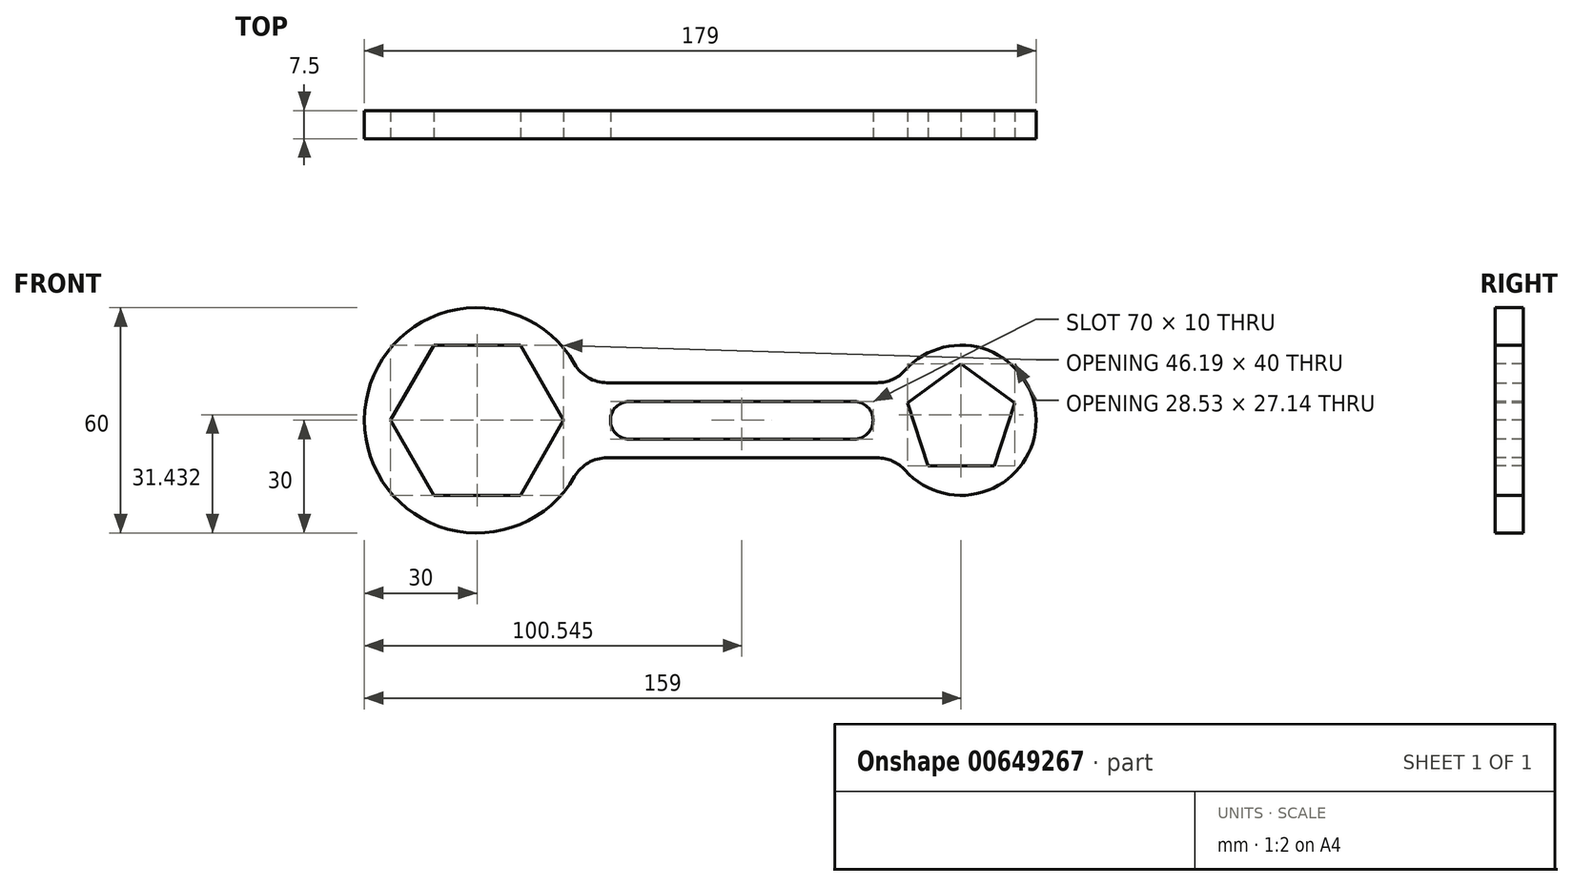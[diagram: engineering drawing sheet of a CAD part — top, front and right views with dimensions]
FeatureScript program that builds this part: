
annotation { "Feature Type Name" : "Feature", "Feature Type Description" : "" }
export const myFeature = defineFeature(function(context is Context, id is Id, definition is map)
    precondition{}
    {
        {
            var Q0;
            Q0=qCreatedBy(makeId("Front.planeOp"),FACE);
            var sketch = newSketch(context, id + "F0", { "sketchPlane" : qUnion([Q0])});
            skLineSegment(sketch, "E0.bottom", {"start": v(-64.5, 10) * mm, "end": v(64.5, 10) * mm});
            skLineSegment(sketch, "E0.top", {"start": v(-64.5, -10) * mm, "end": v(64.5, -10) * mm});
            skLineSegment(sketch, "E0.left", {"start": v(-64.5, 10) * mm, "end": v(-64.5, -10) * mm});
            skLineSegment(sketch, "E0.right", {"start": v(64.5, 10) * mm, "end": v(64.5, -10) * mm});
            skPoint(sketch, "E0.middle", {"position": v(0, 0) * mm});
            skCircle(sketch, "E1", {"center": v(-64.5, 0) * mm, "radius": 30 * mm});
            skCircle(sketch, "E2", {"center": v(64.5, 0) * mm, "radius": 20 * mm});
            skSolve(sketch);
        }
        {
            var Q0;
            Q0 = qSketchRegion(id + "F0", true);
            extrude(context, id + "F1", {"entities" : qUnion([Q0]), "depth" : 7.5 * mm, "offsetDistance" : 25 * mm});
        }
        {
            var Q0;
            Q0=makeQuery(id+"F1.opExtrude","CAP_FACE",FACE,{"disambiguationData":[OSD([sQuery(id+"F0.wireOp",EDGE,"E0.bottom"),sQuery(id+"F0.wireOp",EDGE,"E0.top"),sQuery(id+"F0.wireOp",EDGE,"E1"),sQuery(id+"F0.wireOp",EDGE,"E2")])],"isStart":false});
            var sketch = newSketch(context, id + "F2", { "sketchPlane" : qUnion([Q0])});
            skPoint(sketch, "E3", {"position": v(-64.5, 0) * mm});
            skCircle(sketch, "E4.cCircle", {"center": v(-64.5, 0) * mm, "radius": 20 * mm, "construction": true});
            skLineSegment(sketch, "E4.0", {"start": v(-76.05, 20) * mm, "end": v(-52.95, 20) * mm});
            skLineSegment(sketch, "E4.1", {"start": v(-52.95, 20) * mm, "end": v(-41.4, 0) * mm});
            skLineSegment(sketch, "E4.2", {"start": v(-41.4, 0) * mm, "end": v(-52.95, -20) * mm});
            skLineSegment(sketch, "E4.3", {"start": v(-52.95, -20) * mm, "end": v(-76.05, -20) * mm});
            skLineSegment(sketch, "E4.4", {"start": v(-76.05, -20) * mm, "end": v(-87.6, 0) * mm});
            skLineSegment(sketch, "E4.5", {"start": v(-87.6, 0) * mm, "end": v(-76.05, 20) * mm});
            skPoint(sketch, "E4.0.midPoint", {"position": v(-64.5, 20) * mm});
            skSolve(sketch);
        }
        {
            var Q0;
            Q0 = qSketchRegion(id + "F2", true);
            extrude(context, id + "F3", {"entities" : qUnion([Q0]), "operationType" : NewBodyOperationType.REMOVE, "oppositeDirection" : true, "depth" : 25 * mm, "offsetDistance" : 25 * mm});
        }
        {
            var Q0;
            Q0=makeQuery(id+"F1.opExtrude","CAP_FACE",FACE,{"disambiguationData":[OSD([sQuery(id+"F0.wireOp",EDGE,"E0.bottom"),sQuery(id+"F0.wireOp",EDGE,"E0.top"),sQuery(id+"F0.wireOp",EDGE,"E1"),sQuery(id+"F0.wireOp",EDGE,"E2")])],"isStart":false});
            var sketch = newSketch(context, id + "F4", { "sketchPlane" : qUnion([Q0])});
            skPoint(sketch, "E5", {"position": v(64.5, 0) * mm});
            skCircle(sketch, "E6.cCircle", {"center": v(64.5, 0) * mm, "radius": 12.14 * mm, "construction": true});
            skLineSegment(sketch, "E6.0", {"start": v(78.77, 4.64) * mm, "end": v(73.32, -12.14) * mm});
            skLineSegment(sketch, "E6.1", {"start": v(73.32, -12.14) * mm, "end": v(55.68, -12.14) * mm});
            skLineSegment(sketch, "E6.2", {"start": v(55.68, -12.14) * mm, "end": v(50.23, 4.64) * mm});
            skLineSegment(sketch, "E6.3", {"start": v(50.23, 4.64) * mm, "end": v(64.5, 15) * mm});
            skLineSegment(sketch, "E6.4", {"start": v(64.5, 15) * mm, "end": v(78.77, 4.64) * mm});
            skPoint(sketch, "E6.0.midPoint", {"position": v(76.04, -3.75) * mm});
            skSolve(sketch);
        }
        {
            var Q0;
            Q0 = qSketchRegion(id + "F4", true);
            extrude(context, id + "F5", {"entities" : qUnion([Q0]), "operationType" : NewBodyOperationType.REMOVE, "oppositeDirection" : true, "depth" : 25 * mm, "offsetDistance" : 25 * mm});
        }
        {
            var Q0;
            Q0=makeQuery(id+"F1.opExtrude","CAP_FACE",FACE,{"disambiguationData":[OSD([sQuery(id+"F0.wireOp",EDGE,"E0.bottom"),sQuery(id+"F0.wireOp",EDGE,"E0.top"),sQuery(id+"F0.wireOp",EDGE,"E1"),sQuery(id+"F0.wireOp",EDGE,"E2")])],"isStart":false});
            var sketch = newSketch(context, id + "F6", { "sketchPlane" : qUnion([Q0])});
            skLineSegment(sketch, "E7.bottom", {"start": v(-23.95, -5) * mm, "end": v(36.05, -5) * mm});
            skLineSegment(sketch, "E7.top", {"start": v(-23.95, 5) * mm, "end": v(36.05, 5) * mm});
            skLineSegment(sketch, "E7.left", {"start": v(-23.95, -5) * mm, "end": v(-23.95, 5) * mm});
            skLineSegment(sketch, "E7.right", {"start": v(36.05, -5) * mm, "end": v(36.05, 5) * mm});
            skPoint(sketch, "E7.middle", {"position": v(6.05, 0) * mm});
            skArc(sketch, "E8", {"start": v(36.05, -5) * mm, "mid": v(41.05, 0) * mm, "end": v(36.05, 5) * mm});
            skArc(sketch, "E9", {"start": v(-23.95, 5) * mm, "mid": v(-28.95, 0) * mm, "end": v(-23.95, -5) * mm});
            skSolve(sketch);
        }
        {
            var Q0;
            Q0 = qSketchRegion(id + "F6", true);
            extrude(context, id + "F7", {"entities" : qUnion([Q0]), "operationType" : NewBodyOperationType.REMOVE, "oppositeDirection" : true, "depth" : 25 * mm, "offsetDistance" : 25 * mm});
        }
        {
            var Q0;
            Q0=makeQuery(id+"F1.opExtrude","SWEPT_EDGE",EDGE,{"disambiguationData":[OSD([sQuery(id+"F0.wireOp",EDGE,"E0.top"),sQuery(id+"F0.wireOp",EDGE,"E1")])]});
            var Q1;
            Q1=makeQuery(id+"F1.opExtrude","SWEPT_EDGE",EDGE,{"disambiguationData":[OSD([sQuery(id+"F0.wireOp",EDGE,"E0.bottom"),sQuery(id+"F0.wireOp",EDGE,"E2")])]});
            var Q2;
            Q2=makeQuery(id+"F1.opExtrude","SWEPT_EDGE",EDGE,{"disambiguationData":[OSD([sQuery(id+"F0.wireOp",EDGE,"E0.top"),sQuery(id+"F0.wireOp",EDGE,"E2")])]});
            var Q3;
            Q3=makeQuery(id+"F1.opExtrude","SWEPT_EDGE",EDGE,{"disambiguationData":[OSD([sQuery(id+"F0.wireOp",EDGE,"E0.bottom"),sQuery(id+"F0.wireOp",EDGE,"E1")])]});
            fillet(context, id + "F8", {"entities" : qUnion([Q0, Q1, Q2, Q3]), "radius" : 10 * mm, "tangentPropagation" : true, "allowEdgeOverflow" : false});
        }
    });
